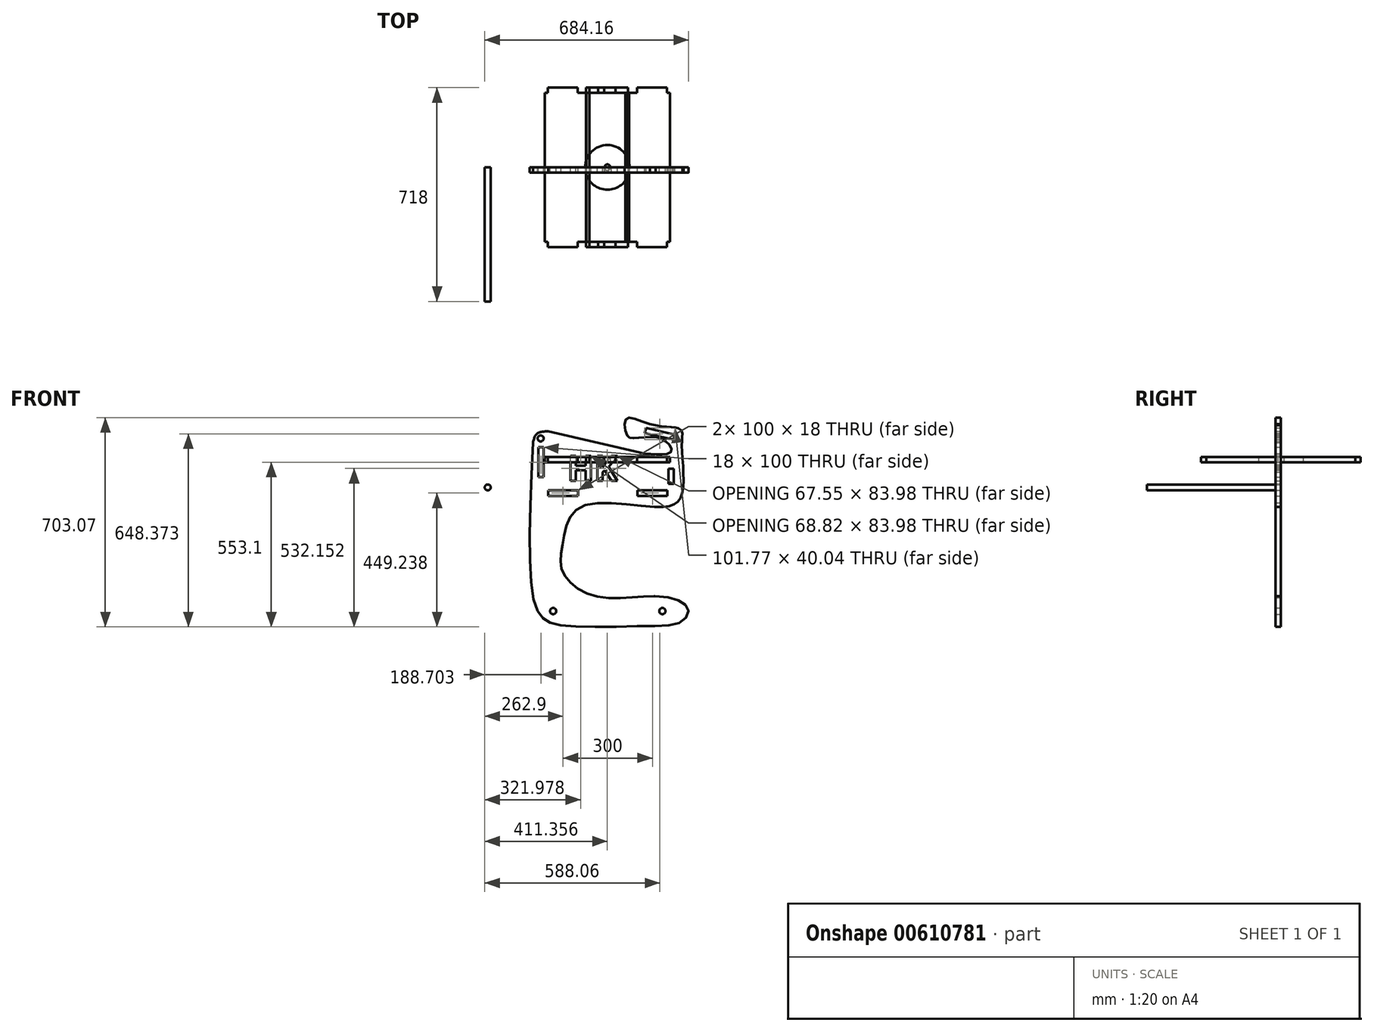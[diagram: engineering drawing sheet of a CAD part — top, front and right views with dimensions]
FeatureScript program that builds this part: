
annotation { "Feature Type Name" : "Feature", "Feature Type Description" : "" }
export const myFeature = defineFeature(function(context is Context, id is Id, definition is map)
    precondition{}
    {
        {
            var Q0;
            Q0=qCreatedBy(makeId("Front.planeOp"),FACE);
            var sketch = newSketch(context, id + "F0", { "sketchPlane" : qUnion([Q0])});
            skLineSegment(sketch, "E0.bottom", {"start": v(187.32, -150) * mm, "end": v(158.28, -150) * mm});
            skPoint(sketch, "E0.middle", {"position": v(0, 0) * mm});
            skLineSegment(sketch, "E1.bottom", {"start": v(-99, -112.86) * mm, "end": v(-199, -112.86) * mm});
            skLineSegment(sketch, "E1.top", {"start": v(-99, -94.86) * mm, "end": v(-199, -94.86) * mm});
            skLineSegment(sketch, "E1.left", {"start": v(-99, -112.86) * mm, "end": v(-99, -94.86) * mm});
            skLineSegment(sketch, "E1.right", {"start": v(-199, -112.86) * mm, "end": v(-199, -94.86) * mm});
            skPoint(sketch, "E1.middle", {"position": v(-149, -103.86) * mm});
            skLineSegment(sketch, "E2.bottom", {"start": v(101, -112.86) * mm, "end": v(201, -112.86) * mm});
            skLineSegment(sketch, "E2.top", {"start": v(101, -94.86) * mm, "end": v(201, -94.86) * mm});
            skLineSegment(sketch, "E2.left", {"start": v(101, -112.86) * mm, "end": v(101, -94.86) * mm});
            skLineSegment(sketch, "E2.right", {"start": v(201, -112.86) * mm, "end": v(201, -94.86) * mm});
            skPoint(sketch, "E2.middle", {"position": v(151, -103.86) * mm});
            skPoint(sketch, "E3.start.orphan", {"position": v(251, -103.86) * mm});
            skLineSegment(sketch, "E4", {"start": v(159.7, -450) * mm, "end": v(156.98, -450) * mm});
            skLineSegment(sketch, "E5", {"start": v(-198.65, 103.64) * mm, "end": v(124.64, 28.96) * mm});
            skPoint(sketch, "E0.top.end.orphan", {"position": v(-250, 150) * mm});
            skPoint(sketch, "E6.orphan", {"position": v(250, 150) * mm});
            skLineSegment(sketch, "E7", {"start": v(161.5, 123.55) * mm, "end": v(142.79, 127.88) * mm});
            skPoint(sketch, "E8.endSnap0", {"position": v(250, 51.55) * mm});
            skPoint(sketch, "E9.orphan", {"position": v(250, 59.96) * mm});
            skLineSegment(sketch, "E10", {"start": v(129.61, 115.3) * mm, "end": v(227.05, 92.79) * mm});
            skPoint(sketch, "E10.startSnap0", {"position": v(103.85, 115.3) * mm});
            skLineSegment(sketch, "E11", {"start": v(227.05, 92.79) * mm, "end": v(223, 75.25) * mm});
            skLineSegment(sketch, "E12", {"start": v(223, 75.25) * mm, "end": v(125.27, 97.82) * mm});
            skLineSegment(sketch, "E13", {"start": v(125.27, 97.82) * mm, "end": v(129.61, 115.3) * mm});
            skLineSegment(sketch, "E14.bottom", {"start": v(-214.2, -50) * mm, "end": v(-232.2, -50) * mm});
            skLineSegment(sketch, "E14.top", {"start": v(-214.2, 50) * mm, "end": v(-232.2, 50) * mm});
            skLineSegment(sketch, "E14.left", {"start": v(-214.2, -50) * mm, "end": v(-214.2, 50) * mm});
            skLineSegment(sketch, "E14.right", {"start": v(-232.2, -50) * mm, "end": v(-232.2, 50) * mm});
            skPoint(sketch, "E14.middle", {"position": v(-223.2, 0) * mm});
            skLineSegment(sketch, "E15.bottom", {"start": v(223.25, -72.44) * mm, "end": v(205.25, -72.44) * mm});
            skLineSegment(sketch, "E15.top", {"start": v(223.25, -22.44) * mm, "end": v(205.25, -22.44) * mm});
            skLineSegment(sketch, "E15.left", {"start": v(223.25, -72.44) * mm, "end": v(223.25, -22.44) * mm});
            skLineSegment(sketch, "E15.right", {"start": v(205.25, -72.44) * mm, "end": v(205.25, -22.44) * mm});
            skPoint(sketch, "E15.middle", {"position": v(214.25, -47.44) * mm});
            skCircle(sketch, "E16", {"center": v(-182.06, -500) * mm, "radius": 10.5 * mm});
            skCircle(sketch, "E17", {"center": v(184.5, -500) * mm, "radius": 10.5 * mm});
            skFitSpline(sketch, "E18", {"points": [v(-250, 66.1) * mm, v(-235.84, 95.81) * mm, v(-198.65, 103.64) * mm], "startDerivative": vector(19.14, 72.87) * mm, "endDerivative": vector(82.8, 3.06) * mm});
            skPoint(sketch, "E19.5.internal.snap0", {"position": v(159.7, 80.82) * mm});
            skPoint(sketch, "E19.18.internal.snap0", {"position": v(159.7, 80.82) * mm});
            skFitSpline(sketch, "E19", {"points": [v(124.64, 28.96) * mm, v(188.74, 26.46) * mm, v(215.55, 37.94) * mm, v(191.84, 73.4) * mm, v(141.4, 85.04) * mm, v(82.6, 80.82) * mm, v(64.2, 93.72) * mm, v(64.2, 146.76) * mm, v(142.79, 127.88) * mm, v(232.6, 115.3) * mm, v(250, 103.1) * mm, v(250, 59.96) * mm, v(251, -103.86) * mm, v(187.32, -150) * mm, v(-90.07, -150) * mm, v(-150, -270.74) * mm, v(-150, -368.4) * mm, v(-40.54, -450) * mm, v(159.7, -450) * mm, v(250, -470.3) * mm, v(272.24, -500.02) * mm, v(250, -535.4) * mm, v(140.62, -550) * mm, v(-139.6, -550) * mm, v(-213.2, -526.9) * mm, v(-250, -450) * mm, v(-250, 66.1) * mm], "startDerivative": vector(2108.3, -192.6) * mm, "endDerivative": vector(309.4, 6943.74) * mm});
            skPoint(sketch, "E20.orphan", {"position": v(250, -450) * mm});
            skPoint(sketch, "E21.start.orphan", {"position": v(250, -550) * mm});
            skPoint(sketch, "E22.orphan", {"position": v(250, -500) * mm});
            skPoint(sketch, "E23.orphan", {"position": v(250, -150) * mm});
            skPoint(sketch, "E24.orphan", {"position": v(-250, -150) * mm});
            skPoint(sketch, "E25.orphan", {"position": v(215.55, 7.96) * mm});
            skPoint(sketch, "E26.orphan", {"position": v(103.85, 136.87) * mm});
            skPoint(sketch, "E27.orphan", {"position": v(103.85, 93.72) * mm});
            skPoint(sketch, "E28.orphan", {"position": v(215.55, 67.91) * mm});
            skPoint(sketch, "E29.orphan", {"position": v(250, 0) * mm});
            skPoint(sketch, "E30.trimOffspring.end.orphan", {"position": v(-150, -150) * mm});
            skCircle(sketch, "E31", {"center": v(-224.2, 79.85) * mm, "radius": 10 * mm});
            skText(sketch, "E32", { "text": "HK", "fontName": "OpenSans-Bold.ttf"});
            const initialGuessF0  = {"E32": [-0.1349, -0.06294, 1, 0, 0.0847]};
            skSetInitialGuess(sketch, initialGuessF0);
            skSolve(sketch);
        }
        {
            var Q0;
            Q0=qCreatedBy(makeId("Top.planeOp"),FACE);
            var sketch = newSketch(context, id + "F1", { "sketchPlane" : qUnion([Q0])});
            skLineSegment(sketch, "E33.bottom", {"start": v(100, -250) * mm, "end": v(-100, -250) * mm});
            skLineSegment(sketch, "E33.top", {"start": v(100, 250) * mm, "end": v(-100, 250) * mm});
            skPoint(sketch, "E33.middle", {"position": v(0, 0) * mm});
            skLineSegment(sketch, "E34", {"start": v(-200, -250) * mm, "end": v(-200, -268) * mm});
            skLineSegment(sketch, "E35", {"start": v(-200, -268) * mm, "end": v(-100, -268) * mm});
            skLineSegment(sketch, "E36", {"start": v(-100, -268) * mm, "end": v(-100, -250) * mm});
            skLineSegment(sketch, "E37", {"start": v(200, -250) * mm, "end": v(200, -268) * mm});
            skLineSegment(sketch, "E38", {"start": v(200, -268) * mm, "end": v(100, -268) * mm});
            skLineSegment(sketch, "E39", {"start": v(100, -268) * mm, "end": v(100, -250) * mm});
            skLineSegment(sketch, "E40", {"start": v(-200, 250) * mm, "end": v(-200, 268) * mm});
            skLineSegment(sketch, "E41", {"start": v(-200, 268) * mm, "end": v(-100, 268) * mm});
            skLineSegment(sketch, "E42", {"start": v(-100, 268) * mm, "end": v(-100, 250) * mm});
            skLineSegment(sketch, "E43", {"start": v(200, 250) * mm, "end": v(200, 268) * mm});
            skLineSegment(sketch, "E44", {"start": v(200, 268) * mm, "end": v(100, 268) * mm});
            skLineSegment(sketch, "E45", {"start": v(100, 268) * mm, "end": v(100, 250) * mm});
            skLineSegment(sketch, "E46", {"start": v(-200, 250) * mm, "end": v(-210, 250) * mm});
            skLineSegment(sketch, "E47", {"start": v(-210, 250) * mm, "end": v(-210, -250) * mm});
            skLineSegment(sketch, "E48", {"start": v(-210, -250) * mm, "end": v(-200, -250) * mm});
            skLineSegment(sketch, "E49", {"start": v(200, 250) * mm, "end": v(210, 250) * mm});
            skLineSegment(sketch, "E50", {"start": v(210, 250) * mm, "end": v(210, -250) * mm});
            skLineSegment(sketch, "E51", {"start": v(210, -250) * mm, "end": v(200, -250) * mm});
            skSolve(sketch);
        }
        {
            var Q0;
            Q0=makeQuery(id+"F1.imprint","IMPRINT",FACE,{"disambiguationData":[TD([[makeQuery(id+"F1.imprint","IMPRINT",EDGE,{"derivedFrom":sQuery(id+"F1.wireOp",EDGE,"E33.bottom")}),-1.0]])]});
            var sketch = newSketch(context, id + "F2", { "sketchPlane" : qUnion([Q0])});
            skLineSegment(sketch, "E52.bottom", {"start": v(72.4, -250) * mm, "end": v(27.6, -250) * mm});
            skLineSegment(sketch, "E52.top", {"start": v(72.4, 250) * mm, "end": v(27.6, 250) * mm});
            skLineSegment(sketch, "E52.left", {"start": v(72.4, -250) * mm, "end": v(72.4, 250) * mm});
            skLineSegment(sketch, "E52.right", {"start": v(-72.4, -250) * mm, "end": v(-72.4, 250) * mm});
            skPoint(sketch, "E52.middle", {"position": v(0, 0) * mm});
            skLineSegment(sketch, "E53", {"start": v(-72.4, -250) * mm, "end": v(-72.4, -268) * mm});
            skLineSegment(sketch, "E54", {"start": v(-72.4, -268) * mm, "end": v(27.6, -268) * mm});
            skLineSegment(sketch, "E55", {"start": v(27.6, -268) * mm, "end": v(27.6, -250) * mm});
            skLineSegment(sketch, "E56", {"start": v(-72.4, 250) * mm, "end": v(-72.4, 268) * mm});
            skLineSegment(sketch, "E57", {"start": v(-72.4, 268) * mm, "end": v(27.6, 268) * mm});
            skLineSegment(sketch, "E58", {"start": v(27.6, 268) * mm, "end": v(27.6, 250) * mm});
            skSolve(sketch);
        }
        {
            var Q0;
            Q0=makeQuery(id+"F1.imprint","IMPRINT",FACE,{"disambiguationData":[TD([[makeQuery(id+"F1.imprint","IMPRINT",EDGE,{"derivedFrom":sQuery(id+"F1.wireOp",EDGE,"E33.bottom")}),-1.0]])]});
            var sketch = newSketch(context, id + "F3", { "sketchPlane" : qUnion([Q0])});
            skLineSegment(sketch, "E59.bottom", {"start": v(60.33, -250) * mm, "end": v(-10.33, -250) * mm});
            skLineSegment(sketch, "E59.top", {"start": v(60.33, 250) * mm, "end": v(-10.33, 250) * mm});
            skLineSegment(sketch, "E59.left", {"start": v(60.33, -250) * mm, "end": v(60.33, 250) * mm});
            skPoint(sketch, "E59.middle", {"position": v(0, 0) * mm});
            skLineSegment(sketch, "E60", {"start": v(-60.33, 250) * mm, "end": v(-60.33, 268) * mm});
            skLineSegment(sketch, "E61", {"start": v(-60.33, 268) * mm, "end": v(-10.33, 268) * mm});
            skLineSegment(sketch, "E62", {"start": v(-10.33, 268) * mm, "end": v(-10.33, 250) * mm});
            skLineSegment(sketch, "E63", {"start": v(-60.33, -250) * mm, "end": v(-60.33, -268) * mm});
            skLineSegment(sketch, "E64", {"start": v(-60.33, -268) * mm, "end": v(-10.33, -268) * mm});
            skLineSegment(sketch, "E65", {"start": v(-10.33, -268) * mm, "end": v(-10.33, -250) * mm});
            skLineSegment(sketch, "E66", {"start": v(-60.33, 250) * mm, "end": v(-70.33, 250) * mm});
            skLineSegment(sketch, "E67", {"start": v(-70.33, 250) * mm, "end": v(-70.33, -250) * mm});
            skLineSegment(sketch, "E68", {"start": v(-70.33, -250) * mm, "end": v(-60.33, -250) * mm});
            skSolve(sketch);
        }
        {
            var Q0;
            Q0=makeQuery(id+"F1.imprint","IMPRINT",FACE,{"disambiguationData":[TD([[makeQuery(id+"F1.imprint","IMPRINT",EDGE,{"derivedFrom":sQuery(id+"F1.wireOp",EDGE,"E33.bottom")}),-1.0]])]});
            var sketch = newSketch(context, id + "F4", { "sketchPlane" : qUnion([Q0])});
            skLineSegment(sketch, "E69.bottom", {"start": v(69.06, -250) * mm, "end": v(-60.94, -250) * mm});
            skLineSegment(sketch, "E69.top", {"start": v(69.06, 250) * mm, "end": v(-60.94, 250) * mm});
            skLineSegment(sketch, "E69.left", {"start": v(69.06, -250) * mm, "end": v(69.06, 250) * mm});
            skLineSegment(sketch, "E69.right", {"start": v(-60.94, -250) * mm, "end": v(-60.94, 250) * mm});
            skPoint(sketch, "E69.middle", {"position": v(4.06, 0) * mm});
            skLineSegment(sketch, "E70", {"start": v(69.06, 250) * mm, "end": v(69.06, 268) * mm});
            skLineSegment(sketch, "E71", {"start": v(69.06, 268) * mm, "end": v(-30.94, 268) * mm});
            skLineSegment(sketch, "E72", {"start": v(-30.94, 268) * mm, "end": v(-30.94, 250) * mm});
            skLineSegment(sketch, "E73", {"start": v(69.06, -250) * mm, "end": v(69.06, -268) * mm});
            skLineSegment(sketch, "E74", {"start": v(69.06, -268) * mm, "end": v(-30.94, -268) * mm});
            skLineSegment(sketch, "E75", {"start": v(-30.94, -268) * mm, "end": v(-30.94, -250) * mm});
            skSolve(sketch);
        }
        {
            var Q0;
            Q0=makeQuery(id+"F1.imprint","IMPRINT",FACE,{"disambiguationData":[TD([[makeQuery(id+"F1.imprint","IMPRINT",EDGE,{"derivedFrom":sQuery(id+"F1.wireOp",EDGE,"E33.bottom")}),-1.0]])]});
            var sketch = newSketch(context, id + "F5", { "sketchPlane" : qUnion([Q0])});
            skCircle(sketch, "E76", {"center": v(0, 0) * mm, "radius": 75 * mm});
            skCircle(sketch, "E77", {"center": v(0, 0) * mm, "radius": 10 * mm});
            skSolve(sketch);
        }
        {
            var Q0;
            Q0 = qSketchRegion(id + "F0", true);
            extrude(context, id + "F6", {"entities" : qUnion([Q0]), "depth" : 18 * mm, "offsetDistance" : 25 * mm});
        }
        {
            var Q0;
            Q0 = qSketchRegion(id + "F1", true);
            extrude(context, id + "F7", {"entities" : qUnion([Q0]), "depth" : 18 * mm, "offsetDistance" : 25 * mm});
        }
        {
            var Q0;
            Q0 = qSketchRegion(id + "F2", true);
            extrude(context, id + "F8", {"entities" : qUnion([Q0]), "depth" : 18 * mm, "offsetDistance" : 25 * mm});
        }
        {
            var Q0;
            Q0 = qSketchRegion(id + "F3", true);
            extrude(context, id + "F9", {"entities" : qUnion([Q0]), "depth" : 18 * mm, "offsetDistance" : 25 * mm});
        }
        {
            var Q0;
            Q0 = qSketchRegion(id + "F4", true);
            extrude(context, id + "F10", {"entities" : qUnion([Q0]), "depth" : 18 * mm, "offsetDistance" : 25 * mm});
        }
        {
            var Q0;
            Q0 = qSketchRegion(id + "F5", true);
            extrude(context, id + "F11", {"entities" : qUnion([Q0]), "depth" : 18 * mm, "offsetDistance" : 25 * mm});
        }
        {
            var Q0;
            Q0=qCreatedBy(makeId("Front.planeOp"),FACE);
            var sketch = newSketch(context, id + "F12", { "sketchPlane" : qUnion([Q0])});
            skCircle(sketch, "E78", {"center": v(-401.9, -84.72) * mm, "radius": 10 * mm});
            skSolve(sketch);
        }
        {
            var Q0;
            Q0 = qSketchRegion(id + "F12", true);
            extrude(context, id + "F13", {"entities" : qUnion([Q0]), "depth" : 450 * mm, "offsetDistance" : 25 * mm});
        }
    });
